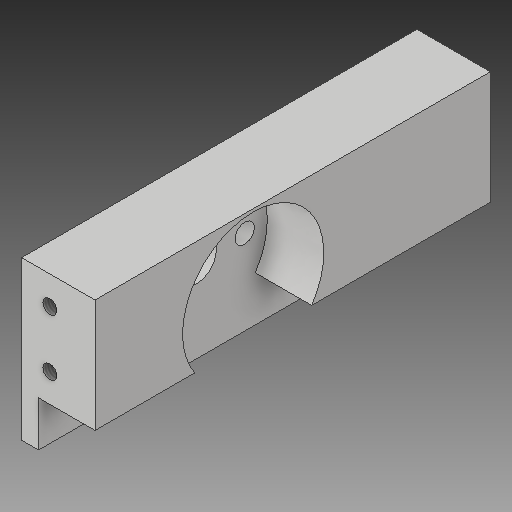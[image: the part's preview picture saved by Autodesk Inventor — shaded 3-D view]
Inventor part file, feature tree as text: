
AUTODESK INVENTOR PART (.ipt)
format: ipt  version: 2019 (Build 230136000, 136)  size: 142,848 bytes
history: native  units: in
note: dims shown in document units (in); Inventor stores cm internally (conversion verified against a paired STEP export)
features: sketch x4, other x3
ambient origin geometry x8: Origin, YZ Plane, XZ Plane, XY Plane, X Axis, Y Axis, Z Axis, Center Point
bodies: Solid1 (feature_tree)
feature tree (7):
  other  "mocowanie silnika.ipt"
  other  "Solid1::mocowanie silnika.ipt"
  other  "TaggingFeature1"
  sketch  "Sketch1"  dims[d0=0.3937in]
  sketch  "Sketch2"
  sketch  "Sketch3"
  sketch  "Sketch4"
